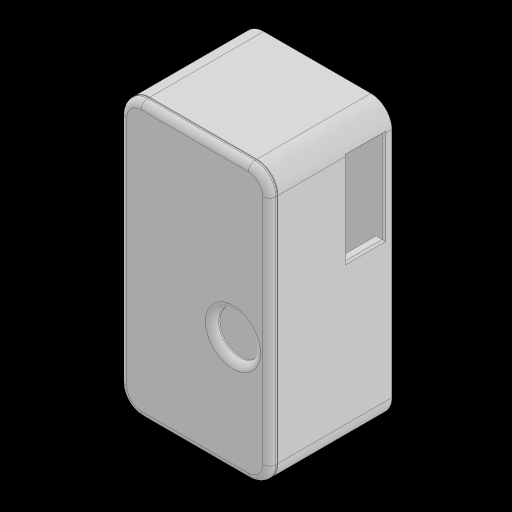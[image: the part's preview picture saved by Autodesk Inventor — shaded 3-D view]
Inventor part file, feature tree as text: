
AUTODESK INVENTOR PART (.ipt)
format: ipt  version: 2024 (Build 280153000, 153)  size: 914,944 bytes
history: native  units: mm
features: sketch x36, extrude x35, projected_geometry x24, chamfer x4, other x3, fillet x3, hole x1, plane x1
ambient origin geometry x8: Origin, YZ Plane, XZ Plane, XY Plane, X Axis, Y Axis, Z Axis, Center Point
bodies: Body1 (feature_tree), Body2 (feature_tree), Body3 (feature_tree)
feature tree (107):
  other  "Main Board"
  extrude  "Extrusion1"  Depth=50.81mm
  hole  "Hole1"  [1 undecoded]
  extrude  "Extrusion2"  Depth=21.45mm
  extrude  "Extrusion3"  Depth=1.65mm
  extrude  "Extrusion4"  Depth=6.6mm
  extrude  "Extrusion5"  Depth=4.2mm
  extrude  "Extrusion6"  Depth=4.2mm
  extrude  "Extrusion7"  Depth=4.6mm TaperAngle=0.0deg
  extrude  "Extrusion8"  Depth=6.0mm
  extrude  "Extrusion9"  Depth=1.7mm
  extrude  "Extrusion10"  Depth=5.6mm TaperAngle=0.0deg
  extrude  "Extrusion11"  Depth=1.6mm TaperAngle=0.0deg
  extrude  "Extrusion12"  Depth=39.3mm
  extrude  "Extrusion13"  Depth=2.86mm
  extrude  "Extrusion14"  Depth=6.0mm TaperAngle=0.0deg
  extrude  "Extrusion15"  Depth=39.3mm
  extrude  "Extrusion16"  Depth=2.84mm
  extrude  "Extrusion17"  Depth=9.2mm
  extrude  "Extrusion18"  Depth=9.2mm
  extrude  "Extrusion19"  Depth=36.43mm
  extrude  "Extrusion20"  Depth=8.0mm
  extrude  "Extrusion21"  Depth=15.91mm
  extrude  "Extrusion22"  Depth=0.08mm
  extrude  "Extrusion23"  Depth=15.91mm
  sketch  "Sketch26"  dims[d67=14.0mm d68=0.0mm d69=0.6mm]
  sketch  "Sketch27"  dims[d70=10.0mm d71=7.82mm d72=12.09mm]
  plane  "Work Plane1"
  extrude  "Extrusion26"  Depth=0.6mm
  extrude  "Extrusion27"  Depth=7.82mm
  fillet  "Fillet2"  Radius=12.09mm
  extrude  "Extrusion29"  Depth=3.73mm
  fillet  "Fillet3"  Radius=3.635mm
  extrude  "Extrusion30"  Depth=16.11mm
  extrude  "Extrusion31"  Depth=14.9mm TaperAngle=0.0deg
  fillet  "Fillet5"  Radius=0.1mm
  extrude  "Extrusion35"  Depth=57.37mm
  chamfer  "Chamfer5"  Distance=2.34mm
  extrude  "Extrusion36"  Depth=1.0mm TaperAngle=0.0deg
  extrude  "Extrusion37"  Depth=24.5mm
  extrude  "Extrusion38"  Depth=0.7mm TaperAngle=0.0deg
  chamfer  "Chamfer6"  Distance=4.0mm
  extrude  "Extrusion39"  Depth=3.0mm
  chamfer  "Chamfer7"  Distance=6.55mm
  extrude  "Extrusion40"  Depth=31.41mm
  extrude  "Extrusion41"  Depth=1.9mm TaperAngle=0.0deg
  chamfer  "Chamfer8"  Distance=3.0mm
  sketch  "Sketch1"  dims[d0=98.33mm d1=50.81mm]
  sketch  "Sketch2"  dims[d2=5.0mm d3=1.54mm d4=0.0mm]
  sketch  "Sketch3"  dims[d5=4.0mm d6=6.0mm d7=4.0mm d8=2.0mm d9=90.0deg d10=8.0mm d11=20.594885mm d12=21.45mm]
  sketch  "Sketch4"  dims[d13=20.1mm d14=1.65mm]
  sketch  "Sketch5"  dims[d15=4.53mm d16=6.6mm]
  sketch  "Sketch6"  dims[d17=4.0mm d18=4.2mm]
  sketch  "Sketch7"  dims[d19=4.0mm d20=4.2mm]
  sketch  "Sketch9"  dims[d22=2.0mm d23=4.6mm d24=0.0mm]
  sketch  "Sketch10"  dims[d25=1.2mm d26=0.0mm d27=6.0mm]
  sketch  "Sketch11"  dims[d28=6.0mm d29=1.7mm]
  sketch  "Sketch12"  dims[d30=15.3mm d31=5.6mm d32=0.0mm]
  sketch  "Sketch13"  dims[d33=3.44mm d34=1.6mm d35=0.0mm]
  projected_geometry  "Projected Loop1"
  projected_geometry  "Projected Loop2"
  sketch  "Sketch14"  dims[d36=17.6mm d37=39.3mm]
  sketch  "Sketch15"  dims[d38=36.46mm d39=2.86mm]
  sketch  "Sketch16"  dims[d40=1.42mm d41=6.0mm d42=0.0mm]
  sketch  "Sketch17"  dims[d43=36.43mm d44=39.3mm]
  sketch  "Sketch18"  dims[d45=1.435mm d46=2.84mm]
  sketch  "Sketch19"  dims[d47=8.4mm d48=0.0mm d49=9.2mm]
  projected_geometry  "Projected Loop3"
  sketch  "Sketch20"  dims[d50=9.2mm d51=9.2mm]
  sketch  "Sketch21"  dims[d53=27.6mm d54=36.43mm]
  sketch  "Sketch22"  dims[d56=4.415mm d57=8.0mm]
  sketch  "Sketch23"  dims[d58=3.75mm d59=0.0mm d60=15.91mm]
  projected_geometry  "Projected Loop4"
  other  "Case"
  sketch  "Sketch24"  dims[d61=16.11mm d62=0.08mm]
  projected_geometry  "Projected Loop5"
  sketch  "Sketch25"  dims[d63=27.55mm d64=15.91mm d65=16.11mm d66=3.71mm]
  projected_geometry  "Projected Loop6"
  projected_geometry  "Projected Loop7"
  projected_geometry  "Projected Loop8"
  projected_geometry  "Projected Loop9"
  projected_geometry  "Projected Loop10"
  projected_geometry  "Projected Loop11"
  projected_geometry  "Projected Loop12"
  sketch  "Sketch28"  dims[d73=4.82mm d74=3.73mm d75=3.635mm]
  projected_geometry  "Projected Loop13"
  other  "Lid"
  sketch  "Sketch29"  dims[d76=2.01mm d77=16.11mm]
  projected_geometry  "Projected Loop14"
  sketch  "Sketch32"  dims[d78=0.05mm]
  projected_geometry  "Projected Loop15"
  projected_geometry  "Projected Loop16"
  sketch  "Sketch34"  dims[d79=7.82mm d80=12.09mm d81=4.82mm d82=3.73mm d83=3.635mm d84=14.9mm d85=0.0mm d86=0.1mm d87=0.0mm]
  projected_geometry  "Projected Loop18"
  sketch  "Sketch35"  dims[d88=2.34mm d89=57.37mm]
  projected_geometry  "Projected Loop19"
  sketch  "Sketch39"  dims[d90=66.48mm]
  projected_geometry  "Projected Loop23"
  sketch  "Sketch40"  dims[d91=3.25mm d92=2.34mm d93=57.37mm d94=22.97mm]
  sketch  "Sketch41"  dims[d95=11.8mm d96=0.0mm d97=1.0mm d98=0.0mm]
  projected_geometry  "Projected Loop24"
  sketch  "Sketch43"  dims[d99=18.0mm d100=24.5mm]
  sketch  "Sketch44"  dims[d101=6.3mm d102=0.7mm d103=0.0mm d104=4.0mm d105=3.0mm d106=6.55mm d107=31.41mm d108=1.9mm d109=0.0mm d110=3.0mm d111=12.8mm d112=35.0mm d113=4.0mm d114=1.9mm d115=0.0mm d116=2.3mm d117=2.3mm d118=0.5mm d119=0.0mm d120=9.0mm d121=3.3mm d122=1.5mm d123=3.7mm d124=9.0mm d125=3.3mm d126=1.5mm d127=2.9mm d128=0.3mm d129=0.3mm d130=7.4mm d131=0.0mm d132=50.0mm d134=2.54mm d135=20.0mm d137=2.54mm d140=2.3mm d141=11.7mm d142=7.4mm d143=0.0mm d144=2.42mm d145=0.0mm d147=1.0mm d148=2.0mm d149=2.0mm d150=0.0mm d151=2.0mm d152=24.36mm d153=0.0mm d154=1.0mm d155=4.0mm d156=0.0mm d157=1.0mm d158=1.0mm d162=7.0mm d163=7.0mm d164=7.0mm d165=7.0mm d174=0.3mm d175=0.8mm d176=10.0mm d177=0.0mm d178=3.0mm d179=0.0mm d180=2.5mm d181=3.5mm d182=3.5mm d190=16.0mm d191=10.0mm d192=0.0mm d193=2.5mm d196=3.0mm d197=14.0mm d198=0.0mm d199=3.0mm d200=0.0mm d201=2.5mm d216=14.0mm d217=35.0mm d218=10.0mm d219=0.0mm d220=0.7mm d221=2.0mm d222=45.0deg d223=45.0deg d224=10.0mm d225=0.0mm d226=10.0mm d227=0.0mm d229=2.0mm d230=2.0mm d231=10.0mm d232=0.0mm d233=0.7mm d234=2.0mm d235=45.0deg d236=1.0mm d237=1.0mm d238=1.0mm d239=1.0mm d240=4.0mm d241=0.0mm d242=0.7mm d243=2.0mm d244=45.0deg d245=2.0mm d246=2.0mm d247=2.0mm d248=2.0mm d249=2.5mm d250=2.5mm d251=2.5mm d252=2.5mm d253=10.0mm d254=0.0mm d255=4.12mm d256=0.0mm d257=0.5mm d258=2.0mm d259=45.0deg d185=0.5mm d186=0.872665mm d187=0.5mm d188=0.872665mm d204=0.5mm d205=0.872665mm d206=0.5mm d207=0.872665mm d208=0.5mm d209=0.872665mm]
  projected_geometry  "Projected Loop25"
  projected_geometry  "Projected Loop26"
  projected_geometry  "Projected Loop27"
  projected_geometry  "Projected Loop28"
note: 1 required parameter value undecoded (feature->parameter linkage not recoverable at this tier; creation-order binding heuristic only, values carry confidence <= 0.55)
